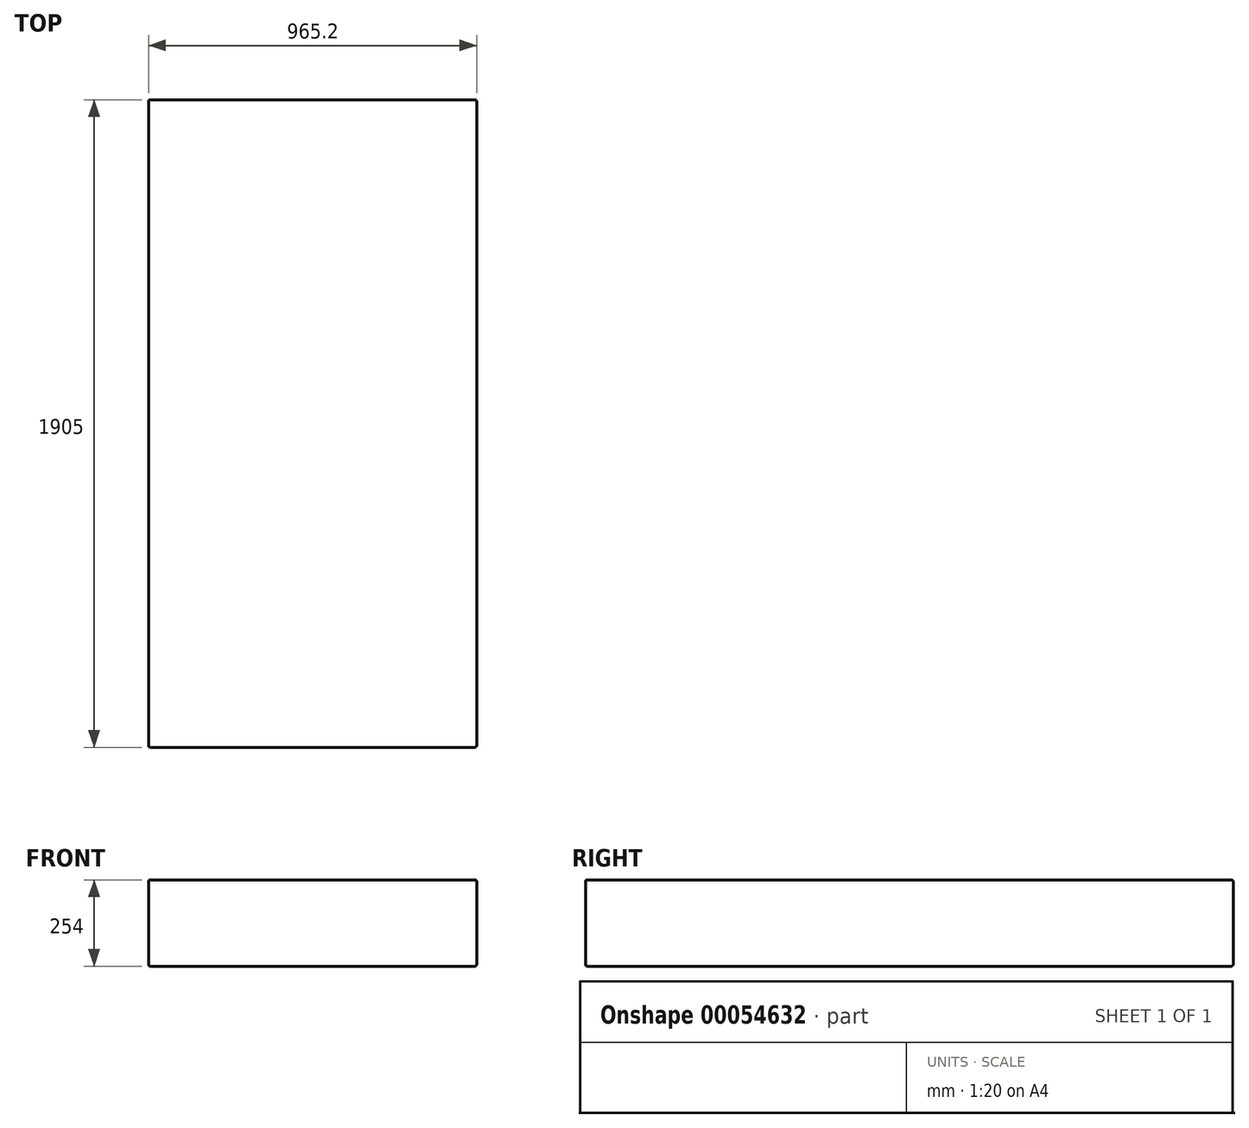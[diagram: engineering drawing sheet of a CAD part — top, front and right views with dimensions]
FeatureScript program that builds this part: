
annotation { "Feature Type Name" : "Feature", "Feature Type Description" : "" }
export const myFeature = defineFeature(function(context is Context, id is Id, definition is map)
    precondition{}
    {
        {
            var Q0;
            Q0=qCreatedBy(makeId("Right.planeOp"),FACE);
            var sketch = newSketch(context, id + "F0", { "sketchPlane" : qUnion([Q0])});
            skLineSegment(sketch, "E0.bottom", {"start": v(0, 0) * mm, "end": v(1905, 0) * mm});
            skLineSegment(sketch, "E0.top", {"start": v(0, 254) * mm, "end": v(1905, 254) * mm});
            skLineSegment(sketch, "E0.left", {"start": v(0, 0) * mm, "end": v(0, 254) * mm});
            skLineSegment(sketch, "E0.right", {"start": v(1905, 0) * mm, "end": v(1905, 254) * mm});
            skSolve(sketch);
        }
        {
            var Q0;
            Q0 = qSketchRegion(id + "F0", true);
            extrude(context, id + "F1", {"entities" : qUnion([Q0]), "endBound" : BoundingType.SYMMETRIC, "depth" : 965.2 * mm});
        }
        {
            var Q0;
            Q0=makeQuery(id+"F1.opExtrude","CAP_EDGE",EDGE,{"disambiguationData":[OSD([sQuery(id+"F0.wireOp",EDGE,"E0.top")])],"isStart":true});
            var Q1;
            Q1=makeQuery(id+"F1.opExtrude","SWEPT_EDGE",EDGE,{"disambiguationData":[OSD([sQuery(id+"F0.wireOp",EDGE,"E0.top"),sQuery(id+"F0.wireOp",EDGE,"E0.left")])]});
            var Q2;
            Q2=makeQuery(id+"F1.opExtrude","SWEPT_EDGE",EDGE,{"disambiguationData":[OSD([sQuery(id+"F0.wireOp",EDGE,"E0.top"),sQuery(id+"F0.wireOp",EDGE,"E0.right")])]});
            var Q3;
            Q3=makeQuery(id+"F1.opExtrude","CAP_EDGE",EDGE,{"disambiguationData":[OSD([sQuery(id+"F0.wireOp",EDGE,"E0.top")])],"isStart":false});
            var Q4;
            Q4=makeQuery(id+"F1.opExtrude","CAP_EDGE",EDGE,{"disambiguationData":[OSD([sQuery(id+"F0.wireOp",EDGE,"E0.left")])],"isStart":true});
            var Q5;
            Q5=makeQuery(id+"F1.opExtrude","CAP_EDGE",EDGE,{"disambiguationData":[OSD([sQuery(id+"F0.wireOp",EDGE,"E0.left")])],"isStart":false});
            var Q6;
            Q6=makeQuery(id+"F1.opExtrude","CAP_EDGE",EDGE,{"disambiguationData":[OSD([sQuery(id+"F0.wireOp",EDGE,"E0.right")])],"isStart":false});
            var Q7;
            Q7=makeQuery(id+"F1.opExtrude","CAP_EDGE",EDGE,{"disambiguationData":[OSD([sQuery(id+"F0.wireOp",EDGE,"E0.bottom")])],"isStart":false});
            var Q8;
            Q8=makeQuery(id+"F1.opExtrude","SWEPT_EDGE",EDGE,{"disambiguationData":[OSD([sQuery(id+"F0.wireOp",EDGE,"E0.bottom"),sQuery(id+"F0.wireOp",EDGE,"E0.left")])]});
            var Q9;
            Q9=makeQuery(id+"F1.opExtrude","SWEPT_EDGE",EDGE,{"disambiguationData":[OSD([sQuery(id+"F0.wireOp",EDGE,"E0.bottom"),sQuery(id+"F0.wireOp",EDGE,"E0.right")])]});
            var Q10;
            Q10=makeQuery(id+"F1.opExtrude","CAP_EDGE",EDGE,{"disambiguationData":[OSD([sQuery(id+"F0.wireOp",EDGE,"E0.right")])],"isStart":true});
            var Q11;
            Q11=makeQuery(id+"F1.opExtrude","CAP_EDGE",EDGE,{"disambiguationData":[OSD([sQuery(id+"F0.wireOp",EDGE,"E0.bottom")])],"isStart":true});
            fillet(context, id + "F2", {"entities" : qUnion([Q0, Q1, Q2, Q3, Q4, Q5, Q6, Q7, Q8, Q9, Q10, Q11]), "radius" : 5.08 * mm, "tangentPropagation" : true, "allowEdgeOverflow" : false});
        }
    });
